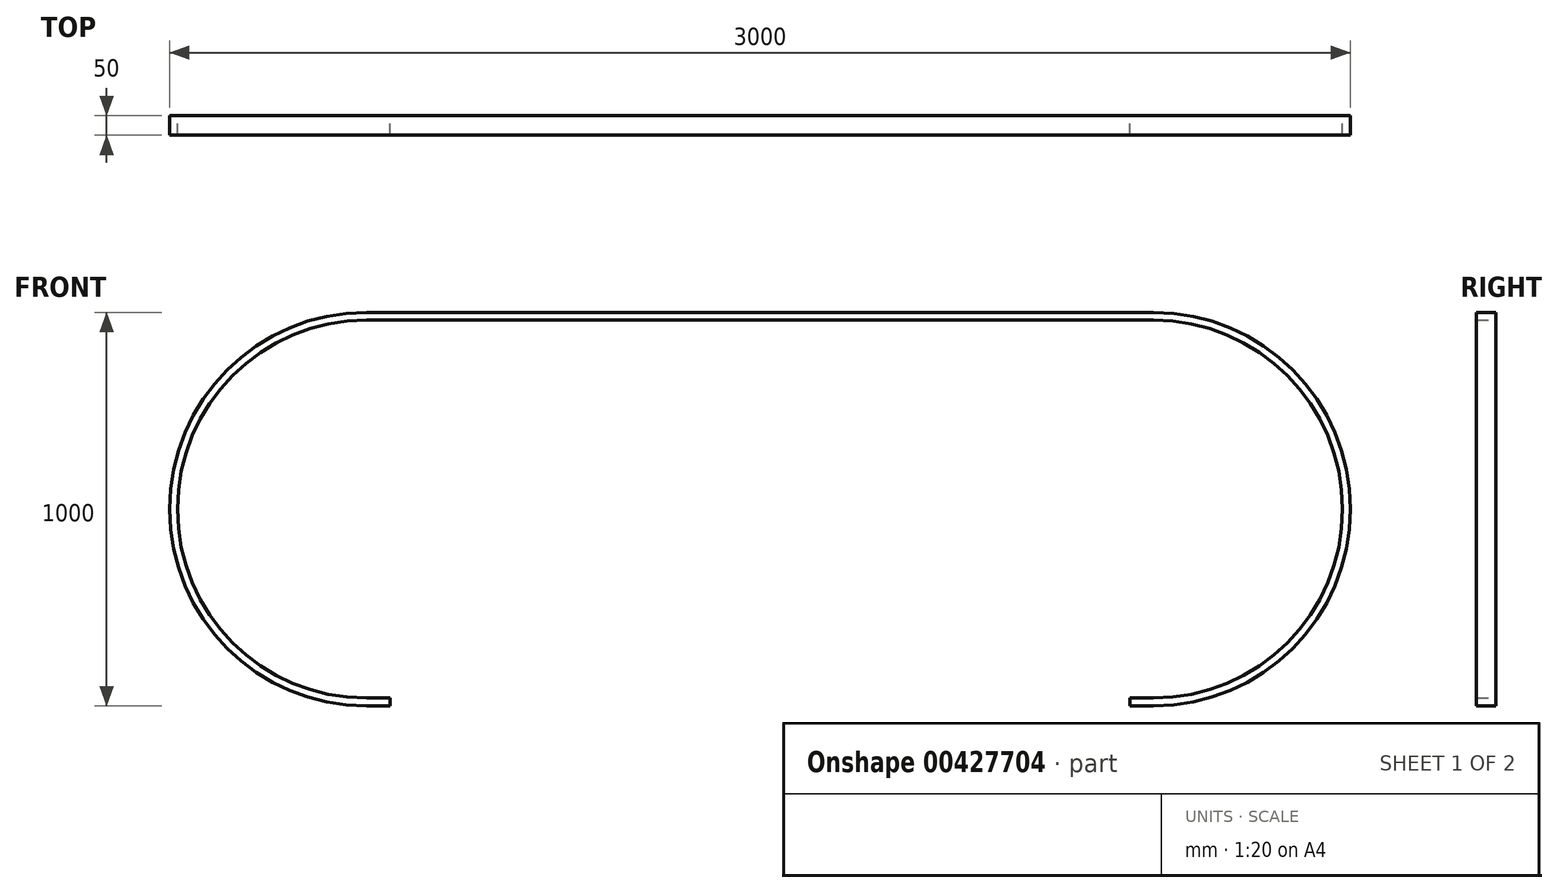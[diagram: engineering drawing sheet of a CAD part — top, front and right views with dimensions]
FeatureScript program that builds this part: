
annotation { "Feature Type Name" : "Feature", "Feature Type Description" : "" }
export const myFeature = defineFeature(function(context is Context, id is Id, definition is map)
    precondition{}
    {
        {
            var Q0;
            Q0=qCreatedBy(makeId("Front.planeOp"),FACE);
            var sketch = newSketch(context, id + "F0", { "sketchPlane" : qUnion([Q0])});
            skLineSegment(sketch, "E0.bottom", {"start": v(-1000, 10) * mm, "end": v(1000, 10) * mm});
            skLineSegment(sketch, "E0.top", {"start": v(-1000, -10) * mm, "end": v(1000, -10) * mm});
            skLineSegment(sketch, "E0.left", {"start": v(-1000, 10) * mm, "end": v(-1000, -10) * mm});
            skLineSegment(sketch, "E0.right", {"start": v(1000, 10) * mm, "end": v(1000, -10) * mm});
            skPoint(sketch, "E0.middle", {"position": v(0, 0) * mm});
            skArc(sketch, "E1", {"start": v(1000, -990) * mm, "mid": v(1500, -490) * mm, "end": v(1000, 10) * mm});
            skLineSegment(sketch, "E2", {"start": v(1000, -490) * mm, "end": v(1000, -10) * mm, "construction": true});
            skArc(sketch, "E3", {"start": v(1000, -970) * mm, "mid": v(1480, -490) * mm, "end": v(1000, -10) * mm});
            skArc(sketch, "E4", {"start": v(-1000, 10) * mm, "mid": v(-1500, -490) * mm, "end": v(-1000, -990) * mm});
            skArc(sketch, "E5", {"start": v(-1000, -10) * mm, "mid": v(-1480, -490) * mm, "end": v(-1000, -970) * mm});
            skLineSegment(sketch, "E6", {"start": v(-1000, -490) * mm, "end": v(-1000, -10) * mm, "construction": true});
            skLineSegment(sketch, "E7", {"start": v(-1000, -490) * mm, "end": v(-1000, -990) * mm, "construction": true});
            skLineSegment(sketch, "E8", {"start": v(-1000, -990) * mm, "end": v(-940, -990) * mm});
            skLineSegment(sketch, "E9", {"start": v(-940, -990) * mm, "end": v(-940, -970) * mm});
            skLineSegment(sketch, "E10", {"start": v(-940, -970) * mm, "end": v(-1000, -970) * mm});
            skLineSegment(sketch, "E11", {"start": v(1000, -490) * mm, "end": v(1000, -990) * mm});
            skLineSegment(sketch, "E12", {"start": v(1000, -990) * mm, "end": v(940, -990) * mm});
            skLineSegment(sketch, "E13", {"start": v(940, -990) * mm, "end": v(940, -970) * mm});
            skLineSegment(sketch, "E14", {"start": v(940, -970) * mm, "end": v(1000, -970) * mm});
            skSolve(sketch);
        }
        {
            var Q0;
            Q0=qSketchRegion(id+"F0",true);
            extrude(context, id + "F1", {"entities" : qUnion([Q0]), "depth" : 50 * mm});
        }
    });
